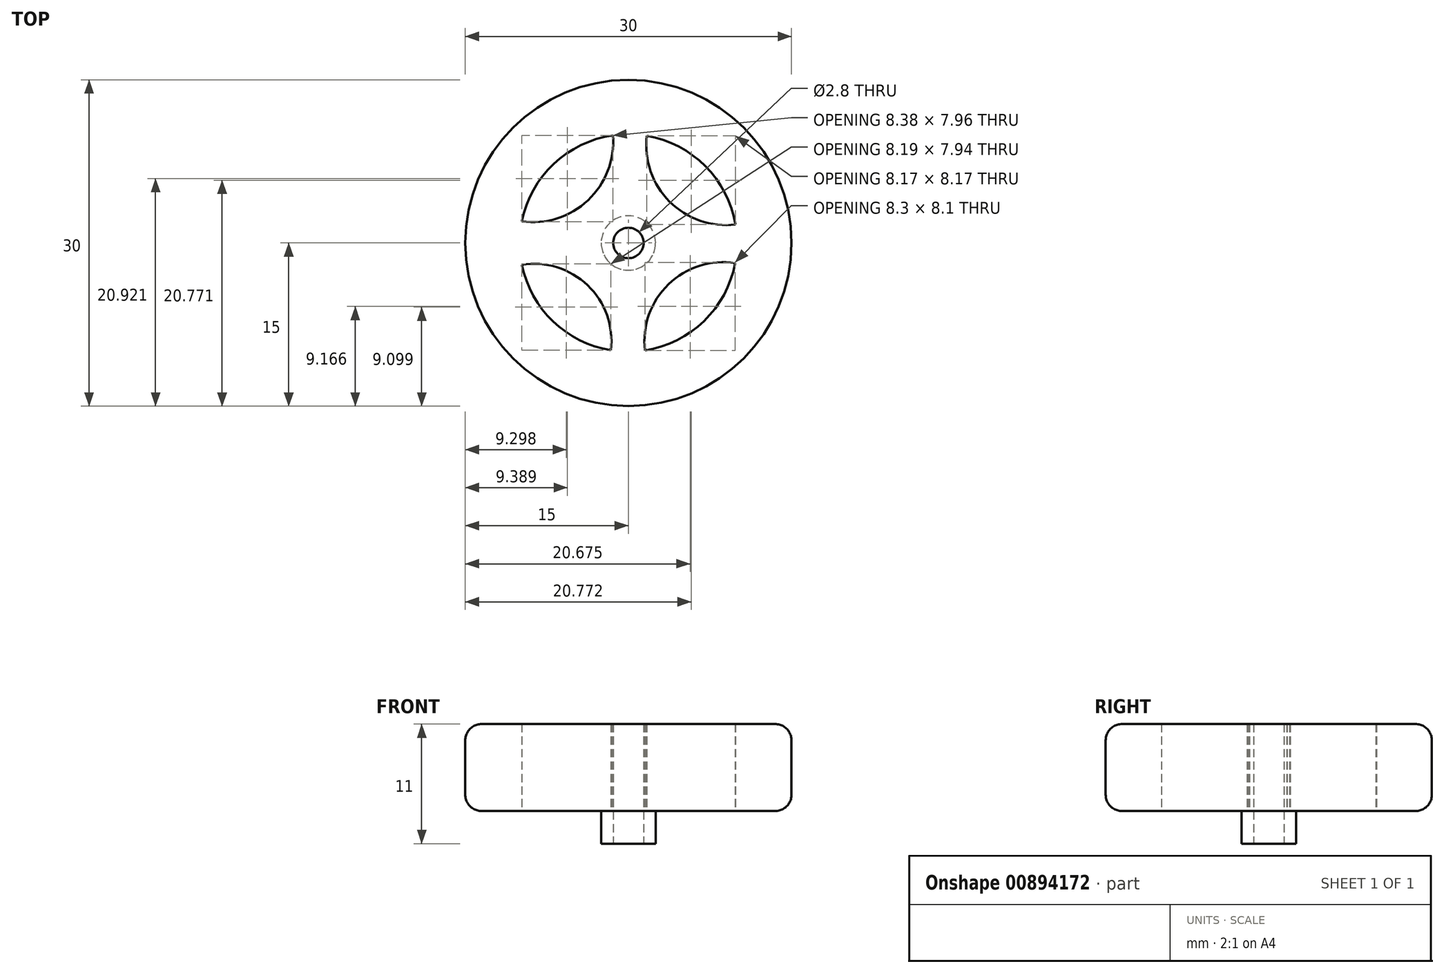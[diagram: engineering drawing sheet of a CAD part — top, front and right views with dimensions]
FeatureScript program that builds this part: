
annotation { "Feature Type Name" : "Feature", "Feature Type Description" : "" }
export const myFeature = defineFeature(function(context is Context, id is Id, definition is map)
    precondition{}
    {
        {
            var Q0;
            Q0=qCreatedBy(makeId("Top.planeOp"),FACE);
            var sketch = newSketch(context, id + "F0", { "sketchPlane" : qUnion([Q0])});
            skCircle(sketch, "E0", {"center": v(0, 0) * mm, "radius": 15 * mm});
            skArc(sketch, "E1", {"start": v(-1.42, 9.9) * mm, "mid": v(-6.87, 7.27) * mm, "end": v(-9.8, 1.99) * mm});
            skCircle(sketch, "E2", {"center": v(0, 0) * mm, "radius": 1.4 * mm});
            skArc(sketch, "E3", {"start": v(-9.8, 1.99) * mm, "mid": v(-3.71, 3.93) * mm, "end": v(-1.42, 9.9) * mm});
            skArc(sketch, "E4", {"start": v(1.7, 9.86) * mm, "mid": v(3.8, 3.8) * mm, "end": v(9.86, 1.7) * mm});
            skArc(sketch, "E5", {"start": v(9.83, -1.85) * mm, "mid": v(3.69, -3.8) * mm, "end": v(1.53, -9.88) * mm});
            skArc(sketch, "E6", {"start": v(-1.61, -9.87) * mm, "mid": v(-3.74, -3.9) * mm, "end": v(-9.8, -2) * mm});
            skArc(sketch, "E7.trimOffspring", {"start": v(-9.8, -2) * mm, "mid": v(-6.93, -7.21) * mm, "end": v(-1.61, -9.87) * mm});
            skArc(sketch, "E8.trimOffspring", {"start": v(9.86, 1.7) * mm, "mid": v(7.07, 7.07) * mm, "end": v(1.7, 9.86) * mm});
            skArc(sketch, "E9.trimOffspring", {"start": v(1.53, -9.88) * mm, "mid": v(6.96, -7.18) * mm, "end": v(9.83, -1.85) * mm});
            skSolve(sketch);
        }
        {
            var Q0;
            Q0 = qSketchRegion(id + "F0", true);
            extrude(context, id + "F1", {"entities" : qUnion([Q0]), "depth" : 8 * mm, "offsetDistance" : 25 * mm});
        }
        {
            var Q0;
            Q0=makeQuery(id+"F1.opExtrude","CAP_EDGE",EDGE,{"disambiguationData":[OSD([sQuery(id+"F0.wireOp",EDGE,"E0")])],"isStart":false});
            fillet(context, id + "F2", {"entities" : qUnion([Q0]), "radius" : 1.5 * mm, "tangentPropagation" : true, "allowEdgeOverflow" : false});
        }
        {
            var Q0;
            Q0=makeQuery(id+"F1.opExtrude","CAP_EDGE",EDGE,{"disambiguationData":[OSD([sQuery(id+"F0.wireOp",EDGE,"E0")])],"isStart":true});
            fillet(context, id + "F3", {"entities" : qUnion([Q0]), "radius" : 1.5 * mm, "tangentPropagation" : true, "allowEdgeOverflow" : false});
        }
        {
            var Q0;
            Q0=makeQuery(id+"F1.opExtrude","CAP_FACE",FACE,{"disambiguationData":[OSD([sQuery(id+"F0.wireOp",EDGE,"E0"),sQuery(id+"F0.wireOp",EDGE,"E1"),sQuery(id+"F0.wireOp",EDGE,"E2"),sQuery(id+"F0.wireOp",EDGE,"E3"),sQuery(id+"F0.wireOp",EDGE,"E4"),sQuery(id+"F0.wireOp",EDGE,"E5"),sQuery(id+"F0.wireOp",EDGE,"E6"),sQuery(id+"F0.wireOp",EDGE,"E7.trimOffspring"),sQuery(id+"F0.wireOp",EDGE,"E8.trimOffspring"),sQuery(id+"F0.wireOp",EDGE,"E9.trimOffspring")])],"isStart":true});
            var sketch = newSketch(context, id + "F4", { "sketchPlane" : qUnion([Q0])});
            skCircle(sketch, "E10", {"center": v(0, 0) * mm, "radius": 2.5 * mm});
            skSolve(sketch);
        }
        {
            var Q0;
            Q0 = qSketchRegion(id + "F4", true);
            extrude(context, id + "F5", {"entities" : qUnion([Q0]), "operationType" : NewBodyOperationType.ADD, "depth" : 3 * mm, "offsetDistance" : 25 * mm});
        }
        {
            var Q0;
            Q0=makeQuery(id+"F5.opExtrude","CAP_FACE",FACE,{"disambiguationData":[OSD([sQuery(id+"F4.wireOp",EDGE,"E10")])],"isStart":false});
            var sketch = newSketch(context, id + "F6", { "sketchPlane" : qUnion([Q0])});
            skCircle(sketch, "E11", {"center": v(0, 0) * mm, "radius": 1.4 * mm});
            skSolve(sketch);
        }
        {
            var Q0;
            Q0 = qSketchRegion(id + "F6", true);
            extrude(context, id + "F7", {"entities" : qUnion([Q0]), "operationType" : NewBodyOperationType.REMOVE, "oppositeDirection" : true, "depth" : 25 * mm, "offsetDistance" : 25 * mm});
        }
    });
